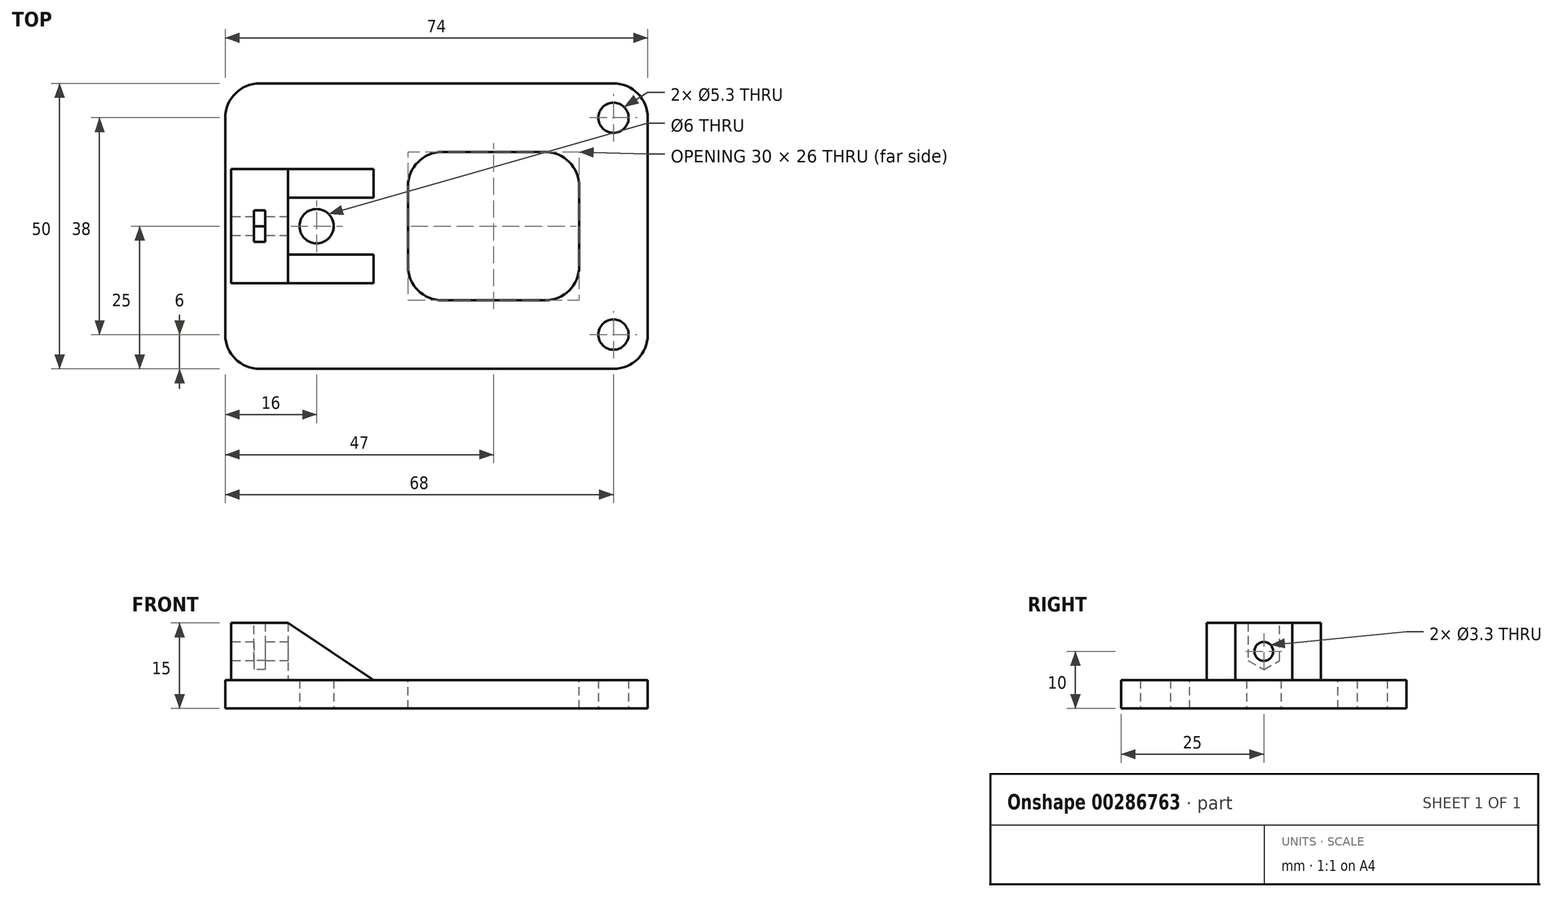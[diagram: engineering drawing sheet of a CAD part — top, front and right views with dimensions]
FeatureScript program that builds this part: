
annotation { "Feature Type Name" : "Feature", "Feature Type Description" : "" }
export const myFeature = defineFeature(function(context is Context, id is Id, definition is map)
    precondition{}
    {
        {
            var Q0;
            Q0=qCreatedBy(makeId("Top.planeOp"),FACE);
            var sketch = newSketch(context, id + "F0", { "sketchPlane" : qUnion([Q0])});
            skLineSegment(sketch, "E0.bottom", {"start": v(0, 0) * mm, "end": v(64, 0) * mm});
            skLineSegment(sketch, "E0.top", {"start": v(0, 50) * mm, "end": v(64, 50) * mm});
            skLineSegment(sketch, "E0.left", {"start": v(0, 0) * mm, "end": v(0, 50) * mm});
            skLineSegment(sketch, "E0.right", {"start": v(64, 0) * mm, "end": v(64, 50) * mm});
            skCircle(sketch, "E1", {"center": v(58, 44) * mm, "radius": 2.65 * mm});
            skPoint(sketch, "E2.centerSnap0", {"position": v(32, 0) * mm});
            skCircle(sketch, "E3", {"center": v(58, 6) * mm, "radius": 2.65 * mm});
            skCircle(sketch, "E4", {"center": v(6, 25) * mm, "radius": 3 * mm});
            skPoint(sketch, "E4.centerSnap0", {"position": v(0, 25) * mm});
            skSolve(sketch);
        }
        {
            var Q0;
            Q0 = qSketchRegion(id + "F0", true);
            extrude(context, id + "F1", {"entities" : qUnion([Q0]), "depth" : 5 * mm});
        }
        {
            var Q0;
            Q0=makeQuery(id+"F1.opExtrude","CAP_FACE",FACE,{"disambiguationData":[OSD([sQuery(id+"F0.wireOp",EDGE,"E0.bottom"),sQuery(id+"F0.wireOp",EDGE,"E0.top"),sQuery(id+"F0.wireOp",EDGE,"E0.left"),sQuery(id+"F0.wireOp",EDGE,"E0.right"),sQuery(id+"F0.wireOp",EDGE,"E1"),sQuery(id+"F0.wireOp",EDGE,"E3"),sQuery(id+"F0.wireOp",EDGE,"E4")])],"isStart":true});
            var sketch = newSketch(context, id + "F2", { "sketchPlane" : qUnion([Q0])});
            skLineSegment(sketch, "E5.bottom", {"start": v(0, -50) * mm, "end": v(-10, -50) * mm});
            skLineSegment(sketch, "E5.top", {"start": v(0, 0) * mm, "end": v(-10, 0) * mm});
            skLineSegment(sketch, "E5.left", {"start": v(0, -50) * mm, "end": v(0, 0) * mm});
            skLineSegment(sketch, "E5.right", {"start": v(-10, -50) * mm, "end": v(-10, 0) * mm});
            skSolve(sketch);
        }
        {
            var Q0;
            Q0 = qSketchRegion(id + "F2", true);
            var Q1;
            Q1=makeQuery(id+"F1.opExtrude","CAP_FACE",FACE,{"disambiguationData":[OSD([sQuery(id+"F0.wireOp",EDGE,"E0.bottom"),sQuery(id+"F0.wireOp",EDGE,"E0.top"),sQuery(id+"F0.wireOp",EDGE,"E0.left"),sQuery(id+"F0.wireOp",EDGE,"E0.right"),sQuery(id+"F0.wireOp",EDGE,"E1"),sQuery(id+"F0.wireOp",EDGE,"E3"),sQuery(id+"F0.wireOp",EDGE,"E4")])],"isStart":false});
            extrude(context, id + "F3", {"entities" : qUnion([Q0]), "operationType" : NewBodyOperationType.ADD, "endBound" : BoundingType.UP_TO_SURFACE, "oppositeDirection" : true, "endBoundEntityFace" : qUnion([Q1]), "depth" : 25 * mm});
        }
        {
            var Q0;
            Q0=makeQuery(id+"F3.boolean.opBoolean","MERGE",FACE,{"derivedFrom":[makeQuery(id+"F1.opExtrude","CAP_FACE",FACE,{"disambiguationData":[OSD([sQuery(id+"F0.wireOp",EDGE,"E0.bottom"),sQuery(id+"F0.wireOp",EDGE,"E0.top"),sQuery(id+"F0.wireOp",EDGE,"E0.left"),sQuery(id+"F0.wireOp",EDGE,"E0.right"),sQuery(id+"F0.wireOp",EDGE,"E1"),sQuery(id+"F0.wireOp",EDGE,"E3"),sQuery(id+"F0.wireOp",EDGE,"E4")])],"isStart":true}),makeQuery(id+"F3.opExtrude","CAP_FACE",FACE,{"disambiguationData":[OSD([sQuery(id+"F2.wireOp",EDGE,"5DGxwNrD-MpHy-m1dG-ja2U-H03dTcWAvzIt"),sQuery(id+"F2.wireOp",EDGE,"aYDKFZU0-LlKQ-FOb0-aPwV-EeLXyGJ3SR0H"),sQuery(id+"F2.wireOp",EDGE,"FAwWxUa0-vHqK-4yEo-Qhqn-bPPlM5ZjcSlq"),sQuery(id+"F2.wireOp",EDGE,"S8Tt7Snn-rHq2-uNbq-wSqk-6UTWnPKzJx4A")])],"isStart":true})]});
            var sketch = newSketch(context, id + "F4", { "sketchPlane" : qUnion([Q0])});
            skCircle(sketch, "E6", {"center": v(6, -25) * mm, "radius": 2.5 * mm});
            skSolve(sketch);
        }
        {
            var Q0;
            {var subQ0=sQuery(id+"F0.wireOp",EDGE,"E4");var subQ1=sQuery(id+"F0.wireOp",EDGE,"E3");var subQ2=sQuery(id+"F0.wireOp",EDGE,"E1");var subQ3=sQuery(id+"F0.wireOp",EDGE,"E0.right");var subQ4=sQuery(id+"F0.wireOp",EDGE,"E0.left");var subQ5=sQuery(id+"F0.wireOp",EDGE,"E0.top");var subQ6=sQuery(id+"F0.wireOp",EDGE,"E0.bottom");Q0=makeQuery(id+"F3.boolean.opBoolean","MERGE",FACE,{"derivedFrom":[makeQuery(id+"F1.opExtrude","CAP_FACE",FACE,{"disambiguationData":[OSD([subQ6,subQ5,subQ4,subQ3,subQ2,subQ1,subQ0])],"isStart":false}),makeQuery(id+"F3.opExtrude","CAP_FACE",FACE,{"disambiguationData":[OSD([subQ6,subQ5,subQ4,subQ3,subQ2,subQ1,subQ0])],"isStart":false})]});}
            var sketch = newSketch(context, id + "F5", { "sketchPlane" : qUnion([Q0])});
            skArc(sketch, "E7", {"start": v(6, 28) * mm, "mid": v(3, 25) * mm, "end": v(6, 22) * mm});
            skLineSegment(sketch, "E8.bottom", {"start": v(6, 30) * mm, "end": v(1, 30) * mm});
            skLineSegment(sketch, "E8.top", {"start": v(6, 20) * mm, "end": v(1, 20) * mm});
            skLineSegment(sketch, "E8.left", {"start": v(6, 30) * mm, "end": v(6, 28) * mm});
            skLineSegment(sketch, "E8.right", {"start": v(1, 30) * mm, "end": v(1, 20) * mm});
            skLineSegment(sketch, "E9.trimOffspring", {"start": v(6, 22) * mm, "end": v(6, 20) * mm});
            skSolve(sketch);
        }
        {
            var Q0;
            {var subQ0=sQuery(id+"F0.wireOp",EDGE,"E4");var subQ1=sQuery(id+"F0.wireOp",EDGE,"E3");var subQ2=sQuery(id+"F0.wireOp",EDGE,"E1");var subQ3=sQuery(id+"F0.wireOp",EDGE,"E0.right");var subQ4=sQuery(id+"F0.wireOp",EDGE,"E0.left");var subQ5=sQuery(id+"F0.wireOp",EDGE,"E0.top");var subQ6=sQuery(id+"F0.wireOp",EDGE,"E0.bottom");Q0=makeQuery(id+"F3.boolean.opBoolean","MERGE",FACE,{"derivedFrom":[makeQuery(id+"F1.opExtrude","CAP_FACE",FACE,{"disambiguationData":[OSD([subQ6,subQ5,subQ4,subQ3,subQ2,subQ1,subQ0])],"isStart":false}),makeQuery(id+"F3.opExtrude","CAP_FACE",FACE,{"disambiguationData":[OSD([subQ6,subQ5,subQ4,subQ3,subQ2,subQ1,subQ0])],"isStart":false})]});}
            var sketch = newSketch(context, id + "F6", { "sketchPlane" : qUnion([Q0])});
            skLineSegment(sketch, "E10.bottom", {"start": v(1, 26.5) * mm, "end": v(-7, 26.5) * mm});
            skLineSegment(sketch, "E10.top", {"start": v(1, 23.5) * mm, "end": v(-7, 23.5) * mm});
            skLineSegment(sketch, "E10.left", {"start": v(1, 26.5) * mm, "end": v(1, 23.5) * mm});
            skLineSegment(sketch, "E10.right", {"start": v(-7, 26.5) * mm, "end": v(-7, 23.5) * mm});
            skSolve(sketch);
        }
        {
            var Q0;
            Q0=makeQuery(id+"F5.imprint","IMPRINT",FACE,{"disambiguationData":[TD([[makeQuery(id+"F5.imprint","IMPRINT",EDGE,{"derivedFrom":sQuery(id+"F5.wireOp",EDGE,"E7")}),1.0]])]});
            var sketch = newSketch(context, id + "F7", { "sketchPlane" : qUnion([Q0])});
            skLineSegment(sketch, "E11.0.0", {"start": v(64, 50) * mm, "end": v(64, 50) * mm});
            skLineSegment(sketch, "E11.0.4", {"start": v(0, 0) * mm, "end": v(64, 0) * mm, "construction": true});
            skLineSegment(sketch, "E11.0.5", {"start": v(64, 0) * mm, "end": v(64, 50) * mm, "construction": true});
            skLineSegment(sketch, "E12", {"start": v(-9, 35) * mm, "end": v(-9, 15) * mm});
            skLineSegment(sketch, "E13", {"start": v(-9, 15) * mm, "end": v(16, 15) * mm});
            skLineSegment(sketch, "E14", {"start": v(16, 15) * mm, "end": v(16, 20) * mm});
            skLineSegment(sketch, "E15", {"start": v(16, 20) * mm, "end": v(1, 20) * mm});
            skLineSegment(sketch, "E16", {"start": v(1, 20) * mm, "end": v(1, 30) * mm});
            skLineSegment(sketch, "E17", {"start": v(1, 30) * mm, "end": v(16, 30) * mm});
            skLineSegment(sketch, "E18", {"start": v(16, 30) * mm, "end": v(16, 35) * mm});
            skLineSegment(sketch, "E19", {"start": v(16, 35) * mm, "end": v(-9, 35) * mm});
            skCircle(sketch, "E20.0", {"center": v(6, 25) * mm, "radius": 3 * mm, "construction": true});
            skSolve(sketch);
        }
        {
            var Q0;
            Q0 = qSketchRegion(id + "F7", true);
            extrude(context, id + "F8", {"entities" : qUnion([Q0]), "depth" : 10 * mm});
        }
        {
            var Q0;
            Q0=makeQuery(id+"F8.opExtrude","SWEPT_FACE",FACE,{"disambiguationData":[OSD([sQuery(id+"F7.wireOp",EDGE,"E13")])]});
            var sketch = newSketch(context, id + "F9", { "sketchPlane" : qUnion([Q0])});
            skLineSegment(sketch, "E21.0", {"start": v(1, 15) * mm, "end": v(16, 15) * mm});
            skLineSegment(sketch, "E22.0", {"start": v(16, 15) * mm, "end": v(16, 5) * mm});
            skLineSegment(sketch, "E23", {"start": v(16, 5) * mm, "end": v(1, 15) * mm});
            skPoint(sketch, "E24.orphan", {"position": v(-9, 15) * mm});
            skLineSegment(sketch, "E25.0.1", {"start": v(1, 5) * mm, "end": v(1, 15) * mm, "construction": true});
            skLineSegment(sketch, "E25.0.3", {"start": v(1, 15) * mm, "end": v(1, 5) * mm, "construction": true});
            skSolve(sketch);
        }
        {
            var Q0;
            Q0 = qSketchRegion(id + "F9", true);
            extrude(context, id + "F10", {"entities" : qUnion([Q0]), "operationType" : NewBodyOperationType.REMOVE, "endBound" : BoundingType.THROUGH_ALL, "oppositeDirection" : true, "depth" : 25 * mm});
        }
        {
            var Q0;
            Q0=makeQuery(id+"F8.opExtrude","SWEPT_FACE",FACE,{"disambiguationData":[OSD([sQuery(id+"F7.wireOp",EDGE,"E12")])]});
            var sketch = newSketch(context, id + "F11", { "sketchPlane" : qUnion([Q0])});
            skCircle(sketch, "E26", {"center": v(-25, 10) * mm, "radius": 1.65 * mm});
            skPoint(sketch, "E26.centerSnap0", {"position": v(-25, 15) * mm});
            skSolve(sketch);
        }
        {
            var Q0;
            Q0 = qSketchRegion(id + "F11", true);
            extrude(context, id + "F12", {"entities" : qUnion([Q0]), "operationType" : NewBodyOperationType.REMOVE, "endBound" : BoundingType.THROUGH_ALL, "oppositeDirection" : true, "depth" : 25 * mm});
        }
        {
            var Q0;
            Q0=makeQuery(id+"F8.opExtrude","SWEPT_FACE",FACE,{"disambiguationData":[OSD([sQuery(id+"F7.wireOp",EDGE,"E12")])]});
            cPlane(context, id + "F13", {"entities" : qUnion([Q0]), "cplaneType" : CPlaneType.OFFSET, "offset" : 5 * mm, "oppositeDirection" : true, "width" : 150 * mm, "height" : 150 * mm});
        }
        {
            var Q0;
            Q0=qCreatedBy(id+"F13.planeOp",FACE);
            var sketch = newSketch(context, id + "F14", { "sketchPlane" : qUnion([Q0])});
            skLineSegment(sketch, "E27.0.0", {"start": v(-35, 5) * mm, "end": v(-15, 5) * mm, "construction": true});
            skLineSegment(sketch, "E27.0.1", {"start": v(-15, 5) * mm, "end": v(-15, 15) * mm, "construction": true});
            skLineSegment(sketch, "E27.0.2", {"start": v(-15, 15) * mm, "end": v(-35, 15) * mm, "construction": true});
            skLineSegment(sketch, "E27.0.3", {"start": v(-35, 15) * mm, "end": v(-35, 5) * mm, "construction": true});
            skCircle(sketch, "E28.0", {"center": v(-25, 10) * mm, "radius": 1.65 * mm, "construction": true});
            skCircle(sketch, "E29.cCircle", {"center": v(-25, 10) * mm, "radius": 2.75 * mm, "construction": true});
            skLineSegment(sketch, "E29.1", {"start": v(-22.25, 8.41) * mm, "end": v(-25, 6.82) * mm});
            skLineSegment(sketch, "E29.2", {"start": v(-25, 6.82) * mm, "end": v(-27.75, 8.41) * mm});
            skPoint(sketch, "E29.0.midPoint", {"position": v(-22.25, 10) * mm});
            skLineSegment(sketch, "E30", {"start": v(-27.75, 8.41) * mm, "end": v(-27.75, 15) * mm});
            skLineSegment(sketch, "E31", {"start": v(-27.75, 15) * mm, "end": v(-22.25, 15) * mm});
            skLineSegment(sketch, "E32", {"start": v(-22.25, 15) * mm, "end": v(-22.25, 8.41) * mm});
            skSolve(sketch);
        }
        {
            var Q0;
            Q0 = qSketchRegion(id + "F14", true);
            extrude(context, id + "F15", {"entities" : qUnion([Q0]), "operationType" : NewBodyOperationType.REMOVE, "endBound" : BoundingType.SYMMETRIC, "oppositeDirection" : true, "depth" : 2 * mm});
        }
        {
            var Q0;
            {var subQ0=sQuery(id+"F0.wireOp",EDGE,"E0.top");Q0=makeQuery(id+"F3.boolean.opBoolean","MERGE",EDGE,{"derivedFrom":[makeQuery(id+"F1.opExtrude","SWEPT_EDGE",EDGE,{"disambiguationData":[OSD([subQ0,sQuery(id+"F0.wireOp",EDGE,"E0.left")])]}),makeQuery(id+"F3.opExtrude","SWEPT_EDGE",EDGE,{"disambiguationData":[OSD([subQ0,sQuery(id+"F2.wireOp",EDGE,"FAwWxUa0-vHqK-4yEo-Qhqn-bPPlM5ZjcSlq"),sQuery(id+"F2.wireOp",EDGE,"S8Tt7Snn-rHq2-uNbq-wSqk-6UTWnPKzJx4A")])]})]});}
            var Q1;
            Q1=makeQuery(id+"F3.opExtrude","SWEPT_EDGE",EDGE,{"disambiguationData":[OSD([sQuery(id+"F2.wireOp",EDGE,"aYDKFZU0-LlKQ-FOb0-aPwV-EeLXyGJ3SR0H"),sQuery(id+"F2.wireOp",EDGE,"FAwWxUa0-vHqK-4yEo-Qhqn-bPPlM5ZjcSlq")])]});
            var Q2;
            Q2=makeQuery(id+"F1.opExtrude","SWEPT_EDGE",EDGE,{"disambiguationData":[OSD([sQuery(id+"F0.wireOp",EDGE,"E0.top"),sQuery(id+"F0.wireOp",EDGE,"E0.right")])]});
            var Q3;
            Q3=makeQuery(id+"F3.opExtrude","SWEPT_EDGE",EDGE,{"disambiguationData":[OSD([sQuery(id+"F2.wireOp",EDGE,"5DGxwNrD-MpHy-m1dG-ja2U-H03dTcWAvzIt"),sQuery(id+"F2.wireOp",EDGE,"aYDKFZU0-LlKQ-FOb0-aPwV-EeLXyGJ3SR0H")])]});
            var Q4;
            {var subQ0=sQuery(id+"F0.wireOp",EDGE,"E0.bottom");Q4=makeQuery(id+"F3.boolean.opBoolean","MERGE",EDGE,{"derivedFrom":[makeQuery(id+"F1.opExtrude","SWEPT_EDGE",EDGE,{"disambiguationData":[OSD([subQ0,sQuery(id+"F0.wireOp",EDGE,"E0.left")])]}),makeQuery(id+"F3.opExtrude","SWEPT_EDGE",EDGE,{"disambiguationData":[OSD([subQ0,sQuery(id+"F2.wireOp",EDGE,"5DGxwNrD-MpHy-m1dG-ja2U-H03dTcWAvzIt"),sQuery(id+"F2.wireOp",EDGE,"S8Tt7Snn-rHq2-uNbq-wSqk-6UTWnPKzJx4A")])]})]});}
            var Q5;
            Q5=makeQuery(id+"F1.opExtrude","SWEPT_EDGE",EDGE,{"disambiguationData":[OSD([sQuery(id+"F0.wireOp",EDGE,"E0.bottom"),sQuery(id+"F0.wireOp",EDGE,"E0.right")])]});
            var Q6;
            Q6=makeQuery(id+"FZVF1w7cgK3Qwny_3.boolean.opBoolean","COPY",EDGE,{"derivedFrom":makeQuery(id+"FZVF1w7cgK3Qwny_3.opExtrude","SWEPT_EDGE",EDGE,{"disambiguationData":[OSD([sQuery(id+"FFE276qaS2nVDXC_3.wireOp",EDGE,"PTaKAA69-yHmF-vDv6-AbaB-ur1nl1c9b8nN.bottom"),sQuery(id+"FFE276qaS2nVDXC_3.wireOp",EDGE,"PTaKAA69-yHmF-vDv6-AbaB-ur1nl1c9b8nN.left")])]})});
            var Q7;
            Q7=makeQuery(id+"FZVF1w7cgK3Qwny_3.boolean.opBoolean","COPY",EDGE,{"derivedFrom":makeQuery(id+"FZVF1w7cgK3Qwny_3.opExtrude","SWEPT_EDGE",EDGE,{"disambiguationData":[OSD([sQuery(id+"FFE276qaS2nVDXC_3.wireOp",EDGE,"PTaKAA69-yHmF-vDv6-AbaB-ur1nl1c9b8nN.bottom"),sQuery(id+"FFE276qaS2nVDXC_3.wireOp",EDGE,"PTaKAA69-yHmF-vDv6-AbaB-ur1nl1c9b8nN.right")])]})});
            var Q8;
            Q8=makeQuery(id+"FZVF1w7cgK3Qwny_3.boolean.opBoolean","COPY",EDGE,{"derivedFrom":makeQuery(id+"FZVF1w7cgK3Qwny_3.opExtrude","SWEPT_EDGE",EDGE,{"disambiguationData":[OSD([sQuery(id+"FFE276qaS2nVDXC_3.wireOp",EDGE,"PTaKAA69-yHmF-vDv6-AbaB-ur1nl1c9b8nN.top"),sQuery(id+"FFE276qaS2nVDXC_3.wireOp",EDGE,"PTaKAA69-yHmF-vDv6-AbaB-ur1nl1c9b8nN.right")])]})});
            var Q9;
            Q9=makeQuery(id+"FZVF1w7cgK3Qwny_3.boolean.opBoolean","COPY",EDGE,{"derivedFrom":makeQuery(id+"FZVF1w7cgK3Qwny_3.opExtrude","SWEPT_EDGE",EDGE,{"disambiguationData":[OSD([sQuery(id+"FFE276qaS2nVDXC_3.wireOp",EDGE,"PTaKAA69-yHmF-vDv6-AbaB-ur1nl1c9b8nN.top"),sQuery(id+"FFE276qaS2nVDXC_3.wireOp",EDGE,"PTaKAA69-yHmF-vDv6-AbaB-ur1nl1c9b8nN.left")])]})});
            fillet(context, id + "F16", {"entities" : qUnion([Q0, Q1, Q2, Q3, Q4, Q5, Q6, Q7, Q8, Q9]), "radius" : 6 * mm, "tangentPropagation" : true, "allowEdgeOverflow" : false});
        }
        {
            var Q0;
            {var subQ12=sQuery(id+"F6.wireOp",EDGE,"E10.left");Q0=makeQuery(id+"F6.imprint","IMPRINT",FACE,{"disambiguationData":[TD([[makeQuery(id+"F6.imprint","IMPRINT",EDGE,{"derivedFrom":subQ12}),1.0]])]});}
            var sketch = newSketch(context, id + "F17", { "sketchPlane" : qUnion([Q0])});
            skLineSegment(sketch, "E33.bottom", {"start": v(22, 38) * mm, "end": v(52, 38) * mm});
            skLineSegment(sketch, "E33.top", {"start": v(22, 12) * mm, "end": v(52, 12) * mm});
            skLineSegment(sketch, "E33.left", {"start": v(22, 38) * mm, "end": v(22, 12) * mm});
            skLineSegment(sketch, "E33.right", {"start": v(52, 38) * mm, "end": v(52, 12) * mm});
            skSolve(sketch);
        }
        {
            var Q0;
            Q0 = qSketchRegion(id + "F17", true);
            extrude(context, id + "F18", {"entities" : qUnion([Q0]), "operationType" : NewBodyOperationType.REMOVE, "endBound" : BoundingType.THROUGH_ALL, "oppositeDirection" : true, "depth" : 25 * mm});
        }
        {
            var Q0;
            Q0=makeQuery(id+"F18.boolean.opBoolean","COPY",EDGE,{"derivedFrom":makeQuery(id+"F18.opExtrude","SWEPT_EDGE",EDGE,{"disambiguationData":[OSD([sQuery(id+"F17.wireOp",EDGE,"E33.bottom"),sQuery(id+"F17.wireOp",EDGE,"E33.left")])]})});
            var Q1;
            Q1=makeQuery(id+"F18.boolean.opBoolean","COPY",EDGE,{"derivedFrom":makeQuery(id+"F18.opExtrude","SWEPT_EDGE",EDGE,{"disambiguationData":[OSD([sQuery(id+"F17.wireOp",EDGE,"E33.bottom"),sQuery(id+"F17.wireOp",EDGE,"E33.right")])]})});
            var Q2;
            Q2=makeQuery(id+"F18.boolean.opBoolean","COPY",EDGE,{"derivedFrom":makeQuery(id+"F18.opExtrude","SWEPT_EDGE",EDGE,{"disambiguationData":[OSD([sQuery(id+"F17.wireOp",EDGE,"E33.top"),sQuery(id+"F17.wireOp",EDGE,"E33.right")])]})});
            var Q3;
            Q3=makeQuery(id+"F18.boolean.opBoolean","COPY",EDGE,{"derivedFrom":makeQuery(id+"F18.opExtrude","SWEPT_EDGE",EDGE,{"disambiguationData":[OSD([sQuery(id+"F17.wireOp",EDGE,"E33.top"),sQuery(id+"F17.wireOp",EDGE,"E33.left")])]})});
            var Q4;
            Q4=makeQuery(id+"F3.opExtrude","SWEPT_EDGE",EDGE,{"disambiguationData":[OSD([sQuery(id+"F2.wireOp",EDGE,"E5.bottom"),sQuery(id+"F2.wireOp",EDGE,"E5.right")])]});
            var Q5;
            Q5=makeQuery(id+"F3.opExtrude","SWEPT_EDGE",EDGE,{"disambiguationData":[OSD([sQuery(id+"F2.wireOp",EDGE,"E5.top"),sQuery(id+"F2.wireOp",EDGE,"E5.right")])]});
            fillet(context, id + "F19", {"entities" : qUnion([Q0, Q1, Q2, Q3, Q4, Q5]), "radius" : 6 * mm, "tangentPropagation" : true, "allowEdgeOverflow" : false});
        }
    });
